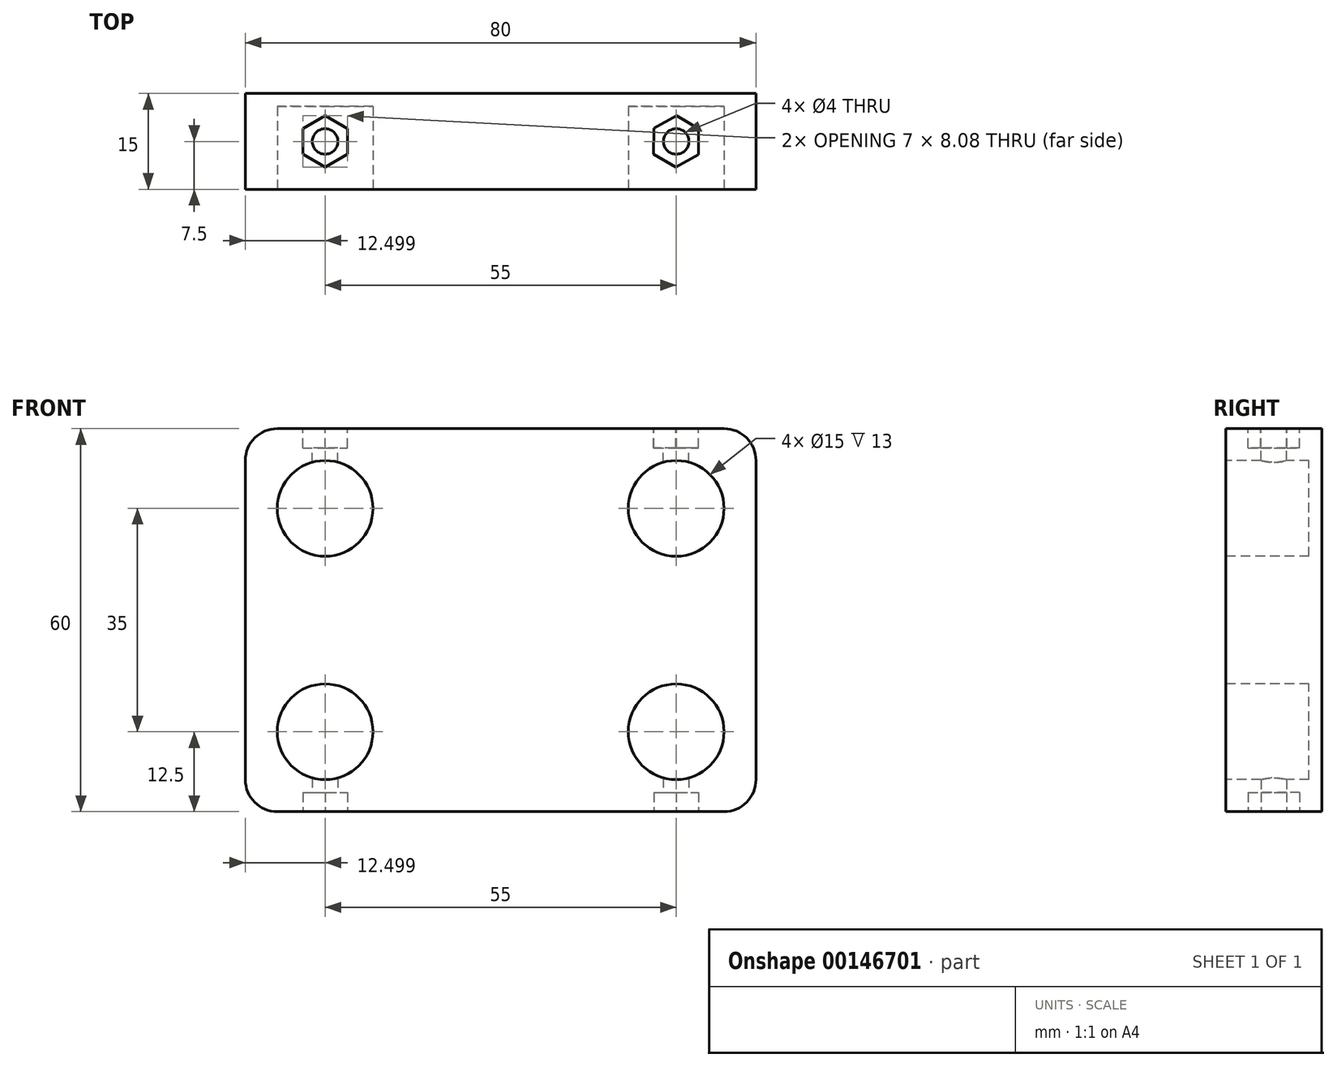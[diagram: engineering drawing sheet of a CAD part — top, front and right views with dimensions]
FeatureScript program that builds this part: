
annotation { "Feature Type Name" : "Feature", "Feature Type Description" : "" }
export const myFeature = defineFeature(function(context is Context, id is Id, definition is map)
    precondition{}
    {
        {
            var Q0;
            Q0=qCreatedBy(makeId("Front.planeOp"),FACE);
            var sketch = newSketch(context, id + "F0", { "sketchPlane" : qUnion([Q0])});
            skLineSegment(sketch, "E0.bottom", {"start": v(-103.38, 18.56) * mm, "end": v(-33.38, 18.56) * mm});
            skLineSegment(sketch, "E0.top", {"start": v(-103.38, -41.44) * mm, "end": v(-33.38, -41.44) * mm});
            skLineSegment(sketch, "E0.left", {"start": v(-108.38, 13.56) * mm, "end": v(-108.38, -36.44) * mm});
            skLineSegment(sketch, "E0.right", {"start": v(-28.38, 13.56) * mm, "end": v(-28.38, -36.44) * mm});
            skArc(sketch, "E1", {"start": v(-103.38, 18.56) * mm, "mid": v(-106.92, 17.1) * mm, "end": v(-108.38, 13.56) * mm});
            skArc(sketch, "E2", {"start": v(-108.38, -36.44) * mm, "mid": v(-106.92, -39.98) * mm, "end": v(-103.38, -41.44) * mm});
            skArc(sketch, "E3", {"start": v(-28.38, 13.56) * mm, "mid": v(-29.85, 17.1) * mm, "end": v(-33.38, 18.56) * mm});
            skArc(sketch, "E4", {"start": v(-33.38, -41.44) * mm, "mid": v(-29.85, -39.98) * mm, "end": v(-28.38, -36.44) * mm});
            skSolve(sketch);
        }
        {
            var Q0;
            Q0 = qSketchRegion(id + "F0", true);
            extrude(context, id + "F1", {"entities" : qUnion([Q0]), "depth" : 15 * mm});
        }
        {
            var Q0;
            Q0=makeQuery(id+"F1.opExtrude","CAP_FACE",FACE,{"disambiguationData":[OSD([sQuery(id+"F0.wireOp",EDGE,"E0.bottom"),sQuery(id+"F0.wireOp",EDGE,"E0.top"),sQuery(id+"F0.wireOp",EDGE,"E0.left"),sQuery(id+"F0.wireOp",EDGE,"E0.right"),sQuery(id+"F0.wireOp",EDGE,"E1"),sQuery(id+"F0.wireOp",EDGE,"E2"),sQuery(id+"F0.wireOp",EDGE,"E3"),sQuery(id+"F0.wireOp",EDGE,"E4")])],"isStart":false});
            var sketch = newSketch(context, id + "F2", { "sketchPlane" : qUnion([Q0])});
            skCircle(sketch, "E5", {"center": v(-95.88, 6.06) * mm, "radius": 7.5 * mm});
            skCircle(sketch, "E6", {"center": v(-95.88, -28.94) * mm, "radius": 7.5 * mm});
            skCircle(sketch, "E7", {"center": v(-40.88, 6.06) * mm, "radius": 7.5 * mm});
            skCircle(sketch, "E8", {"center": v(-40.88, -28.94) * mm, "radius": 7.5 * mm});
            skSolve(sketch);
        }
        {
            var Q0;
            Q0 = qSketchRegion(id + "F2", true);
            extrude(context, id + "F3", {"entities" : qUnion([Q0]), "operationType" : NewBodyOperationType.REMOVE, "oppositeDirection" : true, "depth" : 13 * mm});
        }
        {
            var Q0;
            Q0=makeQuery(id+"F1.opExtrude","SWEPT_FACE",FACE,{"disambiguationData":[OSD([sQuery(id+"F0.wireOp",EDGE,"E0.bottom")])]});
            var sketch = newSketch(context, id + "F4", { "sketchPlane" : qUnion([Q0])});
            skCircle(sketch, "E9", {"center": v(-40.88, -7.5) * mm, "radius": 2 * mm});
            skCircle(sketch, "E10", {"center": v(-95.88, -7.5) * mm, "radius": 2 * mm});
            skSolve(sketch);
        }
        {
            var Q0;
            Q0 = qSketchRegion(id + "F4", true);
            extrude(context, id + "F5", {"entities" : qUnion([Q0]), "operationType" : NewBodyOperationType.REMOVE, "oppositeDirection" : true, "depth" : 6 * mm});
        }
        {
            var Q0;
            Q0=makeQuery(id+"F1.opExtrude","SWEPT_FACE",FACE,{"disambiguationData":[OSD([sQuery(id+"F0.wireOp",EDGE,"E0.bottom")])]});
            var sketch = newSketch(context, id + "F6", { "sketchPlane" : qUnion([Q0])});
            skCircle(sketch, "E11.cCircle", {"center": v(-95.88, -7.5) * mm, "radius": 3.5 * mm, "construction": true});
            skLineSegment(sketch, "E11.0", {"start": v(-92.38, -5.48) * mm, "end": v(-92.38, -9.52) * mm});
            skLineSegment(sketch, "E11.1", {"start": v(-92.38, -9.52) * mm, "end": v(-95.88, -11.54) * mm});
            skLineSegment(sketch, "E11.2", {"start": v(-95.88, -11.54) * mm, "end": v(-99.38, -9.52) * mm});
            skLineSegment(sketch, "E11.3", {"start": v(-99.38, -9.52) * mm, "end": v(-99.38, -5.48) * mm});
            skLineSegment(sketch, "E11.4", {"start": v(-99.38, -5.48) * mm, "end": v(-95.88, -3.46) * mm});
            skLineSegment(sketch, "E11.5", {"start": v(-95.88, -3.46) * mm, "end": v(-92.38, -5.48) * mm});
            skPoint(sketch, "E11.0.midPoint", {"position": v(-92.38, -7.5) * mm});
            skCircle(sketch, "E12.cCircle", {"center": v(-40.88, -7.5) * mm, "radius": 3.5 * mm, "construction": true});
            skLineSegment(sketch, "E12.0", {"start": v(-37.4, -9.56) * mm, "end": v(-40.93, -11.54) * mm});
            skLineSegment(sketch, "E12.1", {"start": v(-40.93, -11.54) * mm, "end": v(-44.4, -9.48) * mm});
            skLineSegment(sketch, "E12.2", {"start": v(-44.4, -9.48) * mm, "end": v(-44.36, -5.44) * mm});
            skLineSegment(sketch, "E12.3", {"start": v(-44.36, -5.44) * mm, "end": v(-40.83, -3.46) * mm});
            skLineSegment(sketch, "E12.4", {"start": v(-40.83, -3.46) * mm, "end": v(-37.36, -5.52) * mm});
            skLineSegment(sketch, "E12.5", {"start": v(-37.36, -5.52) * mm, "end": v(-37.4, -9.56) * mm});
            skPoint(sketch, "E12.0.midPoint", {"position": v(-39.17, -10.55) * mm});
            skSolve(sketch);
        }
        {
            var Q0;
            Q0 = qSketchRegion(id + "F6", true);
            extrude(context, id + "F7", {"entities" : qUnion([Q0]), "operationType" : NewBodyOperationType.REMOVE, "oppositeDirection" : true, "depth" : 3 * mm});
        }
        {
            var Q0;
            Q0=makeQuery(id+"F1.opExtrude","SWEPT_FACE",FACE,{"disambiguationData":[OSD([sQuery(id+"F0.wireOp",EDGE,"E0.top")])]});
            var sketch = newSketch(context, id + "F8", { "sketchPlane" : qUnion([Q0])});
            skCircle(sketch, "E13", {"center": v(-95.88, 7.5) * mm, "radius": 2 * mm});
            skCircle(sketch, "E14", {"center": v(-40.88, 7.5) * mm, "radius": 2 * mm});
            skSolve(sketch);
        }
        {
            var Q0;
            Q0 = qSketchRegion(id + "F8", true);
            extrude(context, id + "F9", {"entities" : qUnion([Q0]), "operationType" : NewBodyOperationType.REMOVE, "oppositeDirection" : true, "depth" : 6 * mm});
        }
        {
            var Q0;
            Q0=makeQuery(id+"F1.opExtrude","SWEPT_FACE",FACE,{"disambiguationData":[OSD([sQuery(id+"F0.wireOp",EDGE,"E0.top")])]});
            var sketch = newSketch(context, id + "F10", { "sketchPlane" : qUnion([Q0])});
            skCircle(sketch, "E15.cCircle", {"center": v(-95.88, 7.5) * mm, "radius": 3.5 * mm, "construction": true});
            skLineSegment(sketch, "E15.0", {"start": v(-92.38, 9.52) * mm, "end": v(-92.38, 5.48) * mm});
            skLineSegment(sketch, "E15.1", {"start": v(-92.38, 5.48) * mm, "end": v(-95.88, 3.46) * mm});
            skLineSegment(sketch, "E15.2", {"start": v(-95.88, 3.46) * mm, "end": v(-99.38, 5.48) * mm});
            skLineSegment(sketch, "E15.3", {"start": v(-99.38, 5.48) * mm, "end": v(-99.38, 9.52) * mm});
            skLineSegment(sketch, "E15.4", {"start": v(-99.38, 9.52) * mm, "end": v(-95.88, 11.54) * mm});
            skLineSegment(sketch, "E15.5", {"start": v(-95.88, 11.54) * mm, "end": v(-92.38, 9.52) * mm});
            skPoint(sketch, "E15.0.midPoint", {"position": v(-92.38, 7.5) * mm});
            skCircle(sketch, "E16.cCircle", {"center": v(-40.88, 7.5) * mm, "radius": 3.5 * mm, "construction": true});
            skLineSegment(sketch, "E16.0", {"start": v(-37.38, 9.52) * mm, "end": v(-37.38, 5.48) * mm});
            skLineSegment(sketch, "E16.1", {"start": v(-37.38, 5.48) * mm, "end": v(-40.88, 3.46) * mm});
            skLineSegment(sketch, "E16.2", {"start": v(-40.88, 3.46) * mm, "end": v(-44.38, 5.48) * mm});
            skLineSegment(sketch, "E16.3", {"start": v(-44.38, 5.48) * mm, "end": v(-44.38, 9.52) * mm});
            skLineSegment(sketch, "E16.4", {"start": v(-44.38, 9.52) * mm, "end": v(-40.88, 11.54) * mm});
            skLineSegment(sketch, "E16.5", {"start": v(-40.88, 11.54) * mm, "end": v(-37.38, 9.52) * mm});
            skPoint(sketch, "E16.0.midPoint", {"position": v(-37.38, 7.5) * mm});
            skSolve(sketch);
        }
        {
            var Q0;
            Q0 = qSketchRegion(id + "F10", true);
            extrude(context, id + "F11", {"entities" : qUnion([Q0]), "operationType" : NewBodyOperationType.REMOVE, "oppositeDirection" : true, "depth" : 3 * mm});
        }
    });
